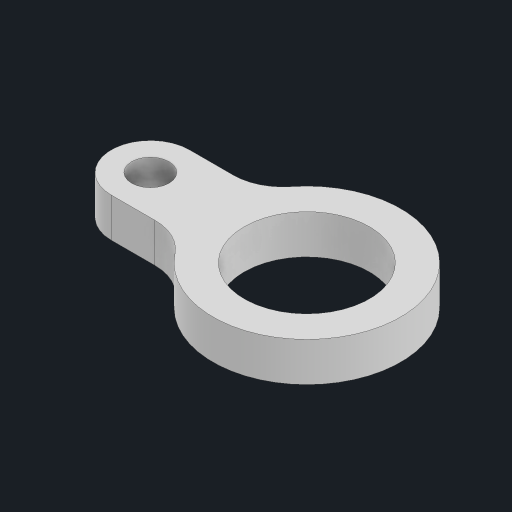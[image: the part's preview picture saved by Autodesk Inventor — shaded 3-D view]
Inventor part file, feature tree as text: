
AUTODESK INVENTOR PART (.ipt)
format: ipt  version: 2023.1 (Build 271208000, 208)  size: 115,712 bytes
history: native  units: mm
features: extrude x1, fillet x1, sketch x1
ambient origin geometry x8: Origin, YZ Plane, XZ Plane, XY Plane, X Axis, Y Axis, Z Axis, Center Point
bodies: Solid1 (feature_tree)
feature tree (3):
  extrude  "Extrusion1"  Depth=20.0mm
  fillet  "Fillet1"  Radius=24.0mm
  sketch  "Sketch1"  dims[d0=16.0mm d1=20.0mm d2=24.0mm d4=10.0mm d5=6.35mm d6=2.25mm d8=5.0mm d9=0.0mm d10=6.35mm]
